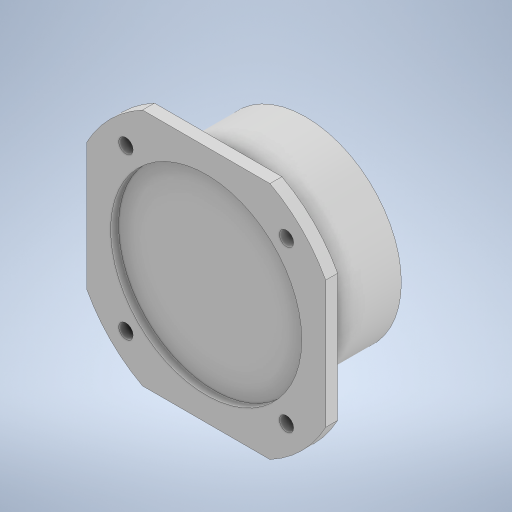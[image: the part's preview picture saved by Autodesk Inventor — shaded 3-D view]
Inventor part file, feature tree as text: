
AUTODESK INVENTOR PART (.ipt)
format: ipt  version: 2023 (Build 270158000, 158)  size: 271,872 bytes
history: native  units: in
note: dims shown in document units (in); Inventor stores cm internally (conversion verified against a paired STEP export)
features: extrude x3, sketch x1
ambient origin geometry x8: Origin, YZ Plane, XZ Plane, XY Plane, X Axis, Y Axis, Z Axis, Center Point
bodies: Solid1 (feature_tree)
feature tree (4):
  sketch  "Sketch1"  dims[d1=1.5748in d2=2.3622in d3=2.3622in d4=2.6772in d5=1.8504in d6=0.315in d7=1.122in d8=0.1417in d9=1.8898in d10=360.0deg d11=2.7559in d12=2.7559in d13=0.1181in d14=0.0in d15=0.0394in d16=0.0in d17=0.8661in d18=0.0in]
  extrude  "Extrusion1"  Depth=0.1181in TaperAngle=0.0deg
  extrude  "Extrusion2"  Depth=0.0394in TaperAngle=0.0deg
  extrude  "Extrusion3"  Depth=0.8661in TaperAngle=0.0deg
